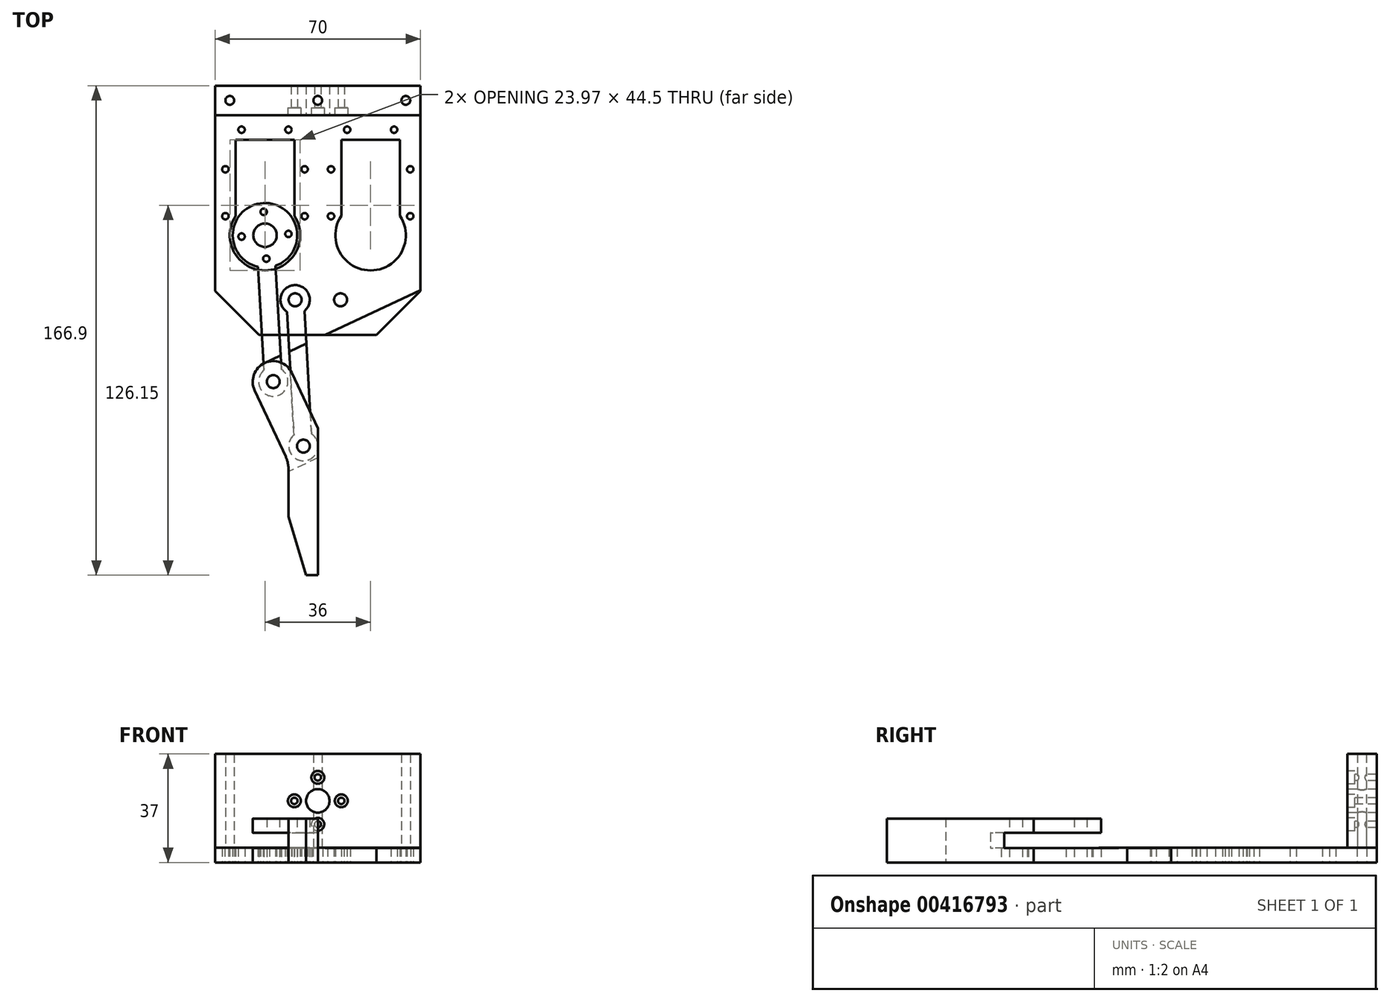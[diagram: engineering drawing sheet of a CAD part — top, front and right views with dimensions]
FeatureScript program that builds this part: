
annotation { "Feature Type Name" : "Feature", "Feature Type Description" : "" }
export const myFeature = defineFeature(function(context is Context, id is Id, definition is map)
    precondition{}
    {
        {
            var Q0;
            Q0=qCreatedBy(makeId("Top.planeOp"),FACE);
            var sketch = newSketch(context, id + "F0", { "sketchPlane" : qUnion([Q0])});
            skLineSegment(sketch, "E0.bottom", {"start": v(15, -15) * mm, "end": v(55, -15) * mm});
            skLineSegment(sketch, "E0.top", {"start": v(0, 70) * mm, "end": v(70, 70) * mm});
            skLineSegment(sketch, "E0.left", {"start": v(0, 0) * mm, "end": v(0, 70) * mm});
            skLineSegment(sketch, "E0.right", {"start": v(70, 0) * mm, "end": v(70, 70) * mm});
            skLineSegment(sketch, "E1.bottom", {"start": v(27, 51.5) * mm, "end": v(7, 51.5) * mm});
            skLineSegment(sketch, "E1.top", {"start": v(27, 25.63) * mm, "end": v(7, 25.63) * mm});
            skLineSegment(sketch, "E1.left", {"start": v(27, 51.5) * mm, "end": v(27, 25.63) * mm});
            skLineSegment(sketch, "E1.right", {"start": v(7, 51.5) * mm, "end": v(7, 25.63) * mm});
            skLineSegment(sketch, "E2", {"start": v(17, 51.5) * mm, "end": v(17, 19) * mm, "construction": true});
            skCircle(sketch, "E3", {"center": v(17, 19) * mm, "radius": 12 * mm});
            skPoint(sketch, "E4", {"position": v(30.5, 25.5) * mm});
            skPoint(sketch, "E5", {"position": v(30.5, 41.5) * mm});
            skPoint(sketch, "E6.MirrorP", {"position": v(3.5, 41.5) * mm});
            skPoint(sketch, "E7.MirrorP", {"position": v(3.5, 25.5) * mm});
            skPoint(sketch, "E8", {"position": v(25, 55) * mm});
            skPoint(sketch, "E9.MirrorP", {"position": v(9, 55) * mm});
            skPoint(sketch, "E10", {"position": v(30.5, 33.5) * mm});
            skPoint(sketch, "E11", {"position": v(30.5, 49.5) * mm});
            skPoint(sketch, "E12", {"position": v(3.5, 49.5) * mm});
            skPoint(sketch, "E13", {"position": v(3.5, 33.5) * mm});
            skLineSegment(sketch, "E14", {"start": v(0, 0) * mm, "end": v(15, -15) * mm});
            skLineSegment(sketch, "E15", {"start": v(55, -15) * mm, "end": v(70, 0) * mm});
            skPoint(sketch, "E16", {"position": v(27.26, -3) * mm});
            skLineSegment(sketch, "E17", {"start": v(35, 70) * mm, "end": v(35, 57.71) * mm, "construction": true});
            skPoint(sketch, "E18.MirrorP", {"position": v(53, 19) * mm});
            skPoint(sketch, "E19.MirrorP", {"position": v(42.74, -3) * mm});
            skPoint(sketch, "E20.MirrorP", {"position": v(66.5, 49.5) * mm});
            skPoint(sketch, "E21.MirrorP", {"position": v(66.5, 41.5) * mm});
            skPoint(sketch, "E22.MirrorP", {"position": v(66.5, 33.5) * mm});
            skPoint(sketch, "E23.MirrorP", {"position": v(66.5, 25.5) * mm});
            skPoint(sketch, "E24.MirrorP", {"position": v(39.5, 25.5) * mm});
            skPoint(sketch, "E25.MirrorP", {"position": v(39.5, 33.5) * mm});
            skPoint(sketch, "E26.MirrorP", {"position": v(39.5, 41.5) * mm});
            skPoint(sketch, "E27.MirrorP", {"position": v(39.5, 49.5) * mm});
            skPoint(sketch, "E28.MirrorP", {"position": v(45, 55) * mm});
            skPoint(sketch, "E29.MirrorP", {"position": v(61, 55) * mm});
            skLineSegment(sketch, "E30.MirrorCS", {"start": v(43, 51.5) * mm, "end": v(63, 51.5) * mm});
            skLineSegment(sketch, "E31.MirrorCS", {"start": v(43, 51.5) * mm, "end": v(43, 25.63) * mm});
            skLineSegment(sketch, "E32.MirrorCS", {"start": v(63, 51.5) * mm, "end": v(63, 25.63) * mm});
            skCircle(sketch, "E33.MirrorC", {"center": v(53, 19) * mm, "radius": 12 * mm});
            skLineSegment(sketch, "E34", {"start": v(27.26, -3) * mm, "end": v(17, 19) * mm, "construction": true});
            skPoint(sketch, "E35", {"position": v(5, 65) * mm});
            skPoint(sketch, "E36", {"position": v(65, 65) * mm});
            skPoint(sketch, "E37", {"position": v(35, 65) * mm});
            skSolve(sketch);
        }
        {
            var Q0;
            Q0 = qSketchRegion(id + "F0", true);
            extrude(context, id + "F1", {"entities" : qUnion([Q0]), "depth" : 5 * mm});
        }
        {
            var Q0;
            Q0=sQuery(id+"F0.wireOp",VERTEX,"E9.MirrorP");
            var Q1;
            Q1=sQuery(id+"F0.wireOp",VERTEX,"E6.MirrorP");
            var Q2;
            Q2=sQuery(id+"F0.wireOp",VERTEX,"E7.MirrorP");
            var Q3;
            Q3=sQuery(id+"F0.wireOp",VERTEX,"E4");
            var Q4;
            Q4=sQuery(id+"F0.wireOp",VERTEX,"E5");
            var Q5;
            Q5=sQuery(id+"F0.wireOp",VERTEX,"E24.MirrorP");
            var Q6;
            Q6=sQuery(id+"F0.wireOp",VERTEX,"E26.MirrorP");
            var Q7;
            Q7=sQuery(id+"F0.wireOp",VERTEX,"E21.MirrorP");
            var Q8;
            Q8=sQuery(id+"F0.wireOp",VERTEX,"E23.MirrorP");
            var Q9;
            Q9=sQuery(id+"F0.wireOp",VERTEX,"E29.MirrorP");
            var Q10;
            Q10=sQuery(id+"F0.wireOp",VERTEX,"E28.MirrorP");
            var Q11;
            Q11=sQuery(id+"F0.wireOp",VERTEX,"E8");
            var Q12;
            Q12=makeQuery(id+"F1.opExtrude","SWEPT_BODY",BODY,{"disambiguationData":[OSD([sQuery(id+"F0.wireOp",EDGE,"E0.bottom"),sQuery(id+"F0.wireOp",EDGE,"E0.top"),sQuery(id+"F0.wireOp",EDGE,"E0.left"),sQuery(id+"F0.wireOp",EDGE,"E0.right"),sQuery(id+"F0.wireOp",EDGE,"E1.bottom"),sQuery(id+"F0.wireOp",EDGE,"E1.left"),sQuery(id+"F0.wireOp",EDGE,"E1.right"),sQuery(id+"F0.wireOp",EDGE,"E14"),sQuery(id+"F0.wireOp",EDGE,"E15"),sQuery(id+"F0.wireOp",EDGE,"E30.MirrorCS"),sQuery(id+"F0.wireOp",EDGE,"E31.MirrorCS"),sQuery(id+"F0.wireOp",EDGE,"E32.MirrorCS"),sQuery(id+"F0.wireOp",EDGE,"E33.MirrorC"),sQuery(id+"F0.wireOp",EDGE,"E3")])]});
            hole(context, id + "F2", {"style" : HoleStyle.SIMPLE, "endStyle" : HoleEndStyle.THROUGH, "oppositeDirection" : true, "holeDiameter" : 2.2 * mm, "isTappedThrough" : true, "tappedDepth" : 6.2 * mm, "tapClearance" : 3, "locations" : qUnion([Q0, Q1, Q2, Q3, Q4, Q5, Q6, Q7, Q8, Q9, Q10, Q11]), "scope" : qUnion([Q12])});
        }
        {
            var Q0;
            Q0=sQuery(id+"F0.wireOp",VERTEX,"E16");
            var Q1;
            Q1=sQuery(id+"F0.wireOp",VERTEX,"E19.MirrorP");
            var Q2;
            Q2=makeQuery(id+"F1.opExtrude","SWEPT_BODY",BODY,{"disambiguationData":[OSD([sQuery(id+"F0.wireOp",EDGE,"E0.bottom"),sQuery(id+"F0.wireOp",EDGE,"E0.top"),sQuery(id+"F0.wireOp",EDGE,"E0.left"),sQuery(id+"F0.wireOp",EDGE,"E0.right"),sQuery(id+"F0.wireOp",EDGE,"E1.bottom"),sQuery(id+"F0.wireOp",EDGE,"E1.left"),sQuery(id+"F0.wireOp",EDGE,"E1.right"),sQuery(id+"F0.wireOp",EDGE,"E14"),sQuery(id+"F0.wireOp",EDGE,"E15"),sQuery(id+"F0.wireOp",EDGE,"E30.MirrorCS"),sQuery(id+"F0.wireOp",EDGE,"E31.MirrorCS"),sQuery(id+"F0.wireOp",EDGE,"E32.MirrorCS"),sQuery(id+"F0.wireOp",EDGE,"E33.MirrorC"),sQuery(id+"F0.wireOp",EDGE,"E3")])]});
            hole(context, id + "F3", {"style" : HoleStyle.SIMPLE, "endStyle" : HoleEndStyle.THROUGH, "oppositeDirection" : true, "standardTappedOrClearance" : lookupTablePath({ "standard" : "ISO", "fit" : "Normal", "size" : "M4", "type" : "Clearance" }), "standardBlindInLast" : lookupTablePath({ "fit" : "Standard", "standard" : "ISO", "size" : "M4", "type" : "Clearance" }), "holeDiameter" : 4.4 * mm, "isTappedThrough" : true, "tappedDepth" : 6.2 * mm, "tapClearance" : 3, "locations" : qUnion([Q0, Q1]), "scope" : qUnion([Q2])});
        }
        {
            var Q0;
            Q0=sQuery(id+"F0.wireOp",VERTEX,"E35");
            var Q1;
            Q1=sQuery(id+"F0.wireOp",VERTEX,"E37");
            var Q2;
            Q2=sQuery(id+"F0.wireOp",VERTEX,"E36");
            var Q3;
            Q3=makeQuery(id+"F1.opExtrude","SWEPT_BODY",BODY,{"disambiguationData":[OSD([sQuery(id+"F0.wireOp",EDGE,"E0.bottom"),sQuery(id+"F0.wireOp",EDGE,"E0.top"),sQuery(id+"F0.wireOp",EDGE,"E0.left"),sQuery(id+"F0.wireOp",EDGE,"E0.right"),sQuery(id+"F0.wireOp",EDGE,"E1.bottom"),sQuery(id+"F0.wireOp",EDGE,"E1.left"),sQuery(id+"F0.wireOp",EDGE,"E1.right"),sQuery(id+"F0.wireOp",EDGE,"E14"),sQuery(id+"F0.wireOp",EDGE,"E15"),sQuery(id+"F0.wireOp",EDGE,"E30.MirrorCS"),sQuery(id+"F0.wireOp",EDGE,"E31.MirrorCS"),sQuery(id+"F0.wireOp",EDGE,"E32.MirrorCS"),sQuery(id+"F0.wireOp",EDGE,"E33.MirrorC"),sQuery(id+"F0.wireOp",EDGE,"E3")])]});
            hole(context, id + "F4", {"style" : HoleStyle.SIMPLE, "endStyle" : HoleEndStyle.THROUGH, "oppositeDirection" : true, "standardTappedOrClearance" : lookupTablePath({ "standard" : "ISO", "fit" : "Normal", "size" : "M3", "type" : "Clearance" }), "standardBlindInLast" : lookupTablePath({ "fit" : "Standard", "standard" : "ISO", "size" : "M3", "type" : "Clearance" }), "holeDiameter" : 3.3 * mm, "isTappedThrough" : true, "tappedDepth" : 6.2 * mm, "tapClearance" : 3, "locations" : qUnion([Q0, Q1, Q2]), "scope" : qUnion([Q3])});
        }
        {
            var Q0;
            Q0=makeQuery(id+"F1.opExtrude","CAP_FACE",FACE,{"disambiguationData":[OSD([sQuery(id+"F0.wireOp",EDGE,"E0.bottom"),sQuery(id+"F0.wireOp",EDGE,"E0.top"),sQuery(id+"F0.wireOp",EDGE,"E0.left"),sQuery(id+"F0.wireOp",EDGE,"E0.right"),sQuery(id+"F0.wireOp",EDGE,"E1.bottom"),sQuery(id+"F0.wireOp",EDGE,"E1.left"),sQuery(id+"F0.wireOp",EDGE,"E1.right"),sQuery(id+"F0.wireOp",EDGE,"E14"),sQuery(id+"F0.wireOp",EDGE,"E15"),sQuery(id+"F0.wireOp",EDGE,"E30.MirrorCS"),sQuery(id+"F0.wireOp",EDGE,"E31.MirrorCS"),sQuery(id+"F0.wireOp",EDGE,"E32.MirrorCS"),sQuery(id+"F0.wireOp",EDGE,"E33.MirrorC"),sQuery(id+"F0.wireOp",EDGE,"E3")])],"isStart":false});
            var sketch = newSketch(context, id + "F5", { "sketchPlane" : qUnion([Q0])});
            skLineSegment(sketch, "E38.bottom", {"start": v(0, 70) * mm, "end": v(70, 70) * mm});
            skLineSegment(sketch, "E38.top", {"start": v(0, 60) * mm, "end": v(70, 60) * mm});
            skLineSegment(sketch, "E38.left", {"start": v(0, 70) * mm, "end": v(0, 60) * mm});
            skLineSegment(sketch, "E38.right", {"start": v(70, 70) * mm, "end": v(70, 60) * mm});
            skCircle(sketch, "E39", {"center": v(5, 65) * mm, "radius": 1.5 * mm});
            skCircle(sketch, "E40", {"center": v(35, 65) * mm, "radius": 1.5 * mm});
            skCircle(sketch, "E41", {"center": v(65, 65) * mm, "radius": 1.5 * mm});
            skSolve(sketch);
        }
        {
            var Q0;
            Q0=makeQuery(id+"F5.imprint","IMPRINT",FACE,{"disambiguationData":[TD([[makeQuery(id+"F5.imprint","IMPRINT",EDGE,{"derivedFrom":sQuery(id+"F5.wireOp",EDGE,"E39")}),-1.0]])]});
            var Q1;
            Q1=makeQuery(id+"F5.imprint","IMPRINT",FACE,{"disambiguationData":[TD([[makeQuery(id+"F5.imprint","IMPRINT",EDGE,{"derivedFrom":sQuery(id+"F5.wireOp",EDGE,"E40")}),-1.0]])]});
            var Q2;
            Q2=makeQuery(id+"F5.imprint","IMPRINT",FACE,{"disambiguationData":[TD([[makeQuery(id+"F5.imprint","IMPRINT",EDGE,{"derivedFrom":sQuery(id+"F5.wireOp",EDGE,"E38.bottom")}),-1.0]])]});
            var Q3;
            Q3=makeQuery(id+"F5.imprint","IMPRINT",FACE,{"disambiguationData":[TD([[makeQuery(id+"F5.imprint","IMPRINT",EDGE,{"derivedFrom":sQuery(id+"F5.wireOp",EDGE,"E41")}),-1.0]])]});
            extrude(context, id + "F6", {"entities" : qUnion([Q0, Q1, Q2, Q3]), "depth" : 32 * mm});
        }
        {
            var Q0;
            Q0=makeQuery(id+"F6.opExtrude","SWEPT_FACE",FACE,{"disambiguationData":[OSD([sQuery(id+"F5.wireOp",EDGE,"E38.top")])]});
            var sketch = newSketch(context, id + "F7", { "sketchPlane" : qUnion([Q0])});
            skCircle(sketch, "E42", {"center": v(35, 21) * mm, "radius": 8 * mm, "construction": true});
            skCircle(sketch, "E43", {"center": v(35, 29) * mm, "radius": 1.1 * mm});
            skCircle(sketch, "E44.1.0", {"center": v(27, 21) * mm, "radius": 1.1 * mm});
            skCircle(sketch, "E44.2.0", {"center": v(35, 13) * mm, "radius": 1.1 * mm});
            skCircle(sketch, "E44.3.0", {"center": v(43, 21) * mm, "radius": 1.1 * mm});
            skCircle(sketch, "E45", {"center": v(35, 21) * mm, "radius": 4 * mm});
            skSolve(sketch);
        }
        {
            var Q0;
            Q0 = qSketchRegion(id + "F7", true);
            extrude(context, id + "F8", {"entities" : qUnion([Q0]), "operationType" : NewBodyOperationType.REMOVE, "endBound" : BoundingType.THROUGH_ALL, "oppositeDirection" : true, "depth" : 25 * mm});
        }
        {
            var Q0;
            Q0=qCreatedBy(makeId("Top.planeOp"),FACE);
            var sketch = newSketch(context, id + "F9", { "sketchPlane" : qUnion([Q0])});
            skLineSegment(sketch, "E46", {"start": v(14, 18.83) * mm, "end": v(16.83, -31.09) * mm});
            skLineSegment(sketch, "E47", {"start": v(16.83, -31.09) * mm, "end": v(22.82, -30.75) * mm});
            skLineSegment(sketch, "E48", {"start": v(22.82, -30.75) * mm, "end": v(20, 19.17) * mm});
            skLineSegment(sketch, "E49", {"start": v(20, 19.17) * mm, "end": v(14, 18.83) * mm});
            skCircle(sketch, "E50", {"center": v(27.26, -3) * mm, "radius": 5 * mm});
            skCircle(sketch, "E51", {"center": v(19.82, -30.92) * mm, "radius": 5 * mm});
            skCircle(sketch, "E52", {"center": v(17, 19) * mm, "radius": 8 * mm, "construction": true});
            skLineSegment(sketch, "E53", {"start": v(24.26, -3.17) * mm, "end": v(30.25, -2.83) * mm});
            skLineSegment(sketch, "E54", {"start": v(24.26, -3.17) * mm, "end": v(27.09, -53.09) * mm});
            skLineSegment(sketch, "E55", {"start": v(27.09, -53.09) * mm, "end": v(33.08, -52.75) * mm});
            skLineSegment(sketch, "E56", {"start": v(33.08, -52.75) * mm, "end": v(30.25, -2.83) * mm});
            skCircle(sketch, "E57", {"center": v(30.08, -52.92) * mm, "radius": 5 * mm});
            skCircle(sketch, "E58.0", {"center": v(27.26, -3) * mm, "radius": 2.2 * mm});
            skCircle(sketch, "E59", {"center": v(30.08, -52.92) * mm, "radius": 2.2 * mm});
            skCircle(sketch, "E60", {"center": v(19.82, -30.92) * mm, "radius": 2.2 * mm});
            skLineSegment(sketch, "E61", {"start": v(30.08, -52.92) * mm, "end": v(19.82, -30.92) * mm, "construction": true});
            skCircle(sketch, "E62", {"center": v(17, 19) * mm, "radius": 11 * mm});
            skLineSegment(sketch, "E63", {"start": v(16.55, 26.99) * mm, "end": v(17.8, 4.71) * mm, "construction": true});
            skCircle(sketch, "E64", {"center": v(17, 19) * mm, "radius": 4 * mm});
            skCircle(sketch, "E65", {"center": v(16.55, 26.99) * mm, "radius": 1.1 * mm});
            skCircle(sketch, "E66.1.0", {"center": v(9.01, 18.55) * mm, "radius": 1.1 * mm});
            skCircle(sketch, "E66.2.0", {"center": v(17.45, 11.01) * mm, "radius": 1.1 * mm});
            skCircle(sketch, "E66.3.0", {"center": v(24.99, 19.45) * mm, "radius": 1.1 * mm});
            skSolve(sketch);
        }
        {
            var Q0;
            Q0=makeQuery(id+"F9.imprint","IMPRINT",FACE,{"disambiguationData":[TD([[makeQuery(id+"F9.imprint","IMPRINT",EDGE,{"derivedFrom":sQuery(id+"F9.wireOp",EDGE,"648b47fd-c98e-4e7c-a0a6-51eef2966ebb.1.0")}),-1.0]])]});
            var Q1;
            {var subQ1=sQuery(id+"F9.wireOp",EDGE,"E47");var subQ7=sQuery(id+"F9.wireOp",EDGE,"E46");var subQ8=makeQuery(id+"F9.imprint","INTERSECT",VERTEX,{"derivedFrom":[subQ7,subQ1]});Q1=makeQuery(id+"F9.imprint","IMPRINT",FACE,{"disambiguationData":[TD([[makeQuery(id+"F9.imprint","IMPRINT",EDGE,{"disambiguationData":[TD([[subQ8,1.0]])],"derivedFrom":subQ7}),-1.0]])]});}
            var Q2;
            {var subQ1=sQuery(id+"F9.wireOp",EDGE,"E47");var subQ7=sQuery(id+"F9.wireOp",EDGE,"E46");var subQ8=makeQuery(id+"F9.imprint","INTERSECT",VERTEX,{"derivedFrom":[subQ7,subQ1]});Q2=makeQuery(id+"F9.imprint","IMPRINT",FACE,{"disambiguationData":[TD([[makeQuery(id+"F9.imprint","IMPRINT",EDGE,{"disambiguationData":[TD([[subQ8,1.0]])],"derivedFrom":subQ7}),1.0]])]});}
            var Q3;
            {var subQ0=sQuery(id+"F9.wireOp",EDGE,"E54");var subQ1=sQuery(id+"F9.wireOp",EDGE,"E50");var subQ2=makeQuery(id+"F9.imprint","INTERSECT",VERTEX,{"derivedFrom":[subQ1,subQ0]});Q3=makeQuery(id+"F9.imprint","IMPRINT",FACE,{"disambiguationData":[TD([[makeQuery(id+"F9.imprint","IMPRINT",EDGE,{"disambiguationData":[TD([[subQ2,-1.0]])],"derivedFrom":subQ1}),-1.0]])]});}
            var Q4;
            {var subQ0=sQuery(id+"F9.wireOp",EDGE,"E54");var subQ3=sQuery(id+"F9.wireOp",EDGE,"E50");var subQ4=makeQuery(id+"F9.imprint","INTERSECT",VERTEX,{"derivedFrom":[subQ3,subQ0]});Q4=makeQuery(id+"F9.imprint","IMPRINT",FACE,{"disambiguationData":[TD([[makeQuery(id+"F9.imprint","IMPRINT",EDGE,{"disambiguationData":[TD([[subQ4,1.0]])],"derivedFrom":subQ3}),1.0]])]});}
            var Q5;
            {var subQ0=sQuery(id+"F9.wireOp",EDGE,"E54");var subQ3=sQuery(id+"F9.wireOp",EDGE,"E50");var subQ4=makeQuery(id+"F9.imprint","INTERSECT",VERTEX,{"derivedFrom":[subQ3,subQ0]});Q5=makeQuery(id+"F9.imprint","IMPRINT",FACE,{"disambiguationData":[TD([[makeQuery(id+"F9.imprint","IMPRINT",EDGE,{"disambiguationData":[TD([[subQ4,-1.0]])],"derivedFrom":subQ3}),1.0]])]});}
            var Q6;
            {var subQ1=sQuery(id+"F9.wireOp",EDGE,"E55");var subQ7=sQuery(id+"F9.wireOp",EDGE,"E54");var subQ8=makeQuery(id+"F9.imprint","INTERSECT",VERTEX,{"derivedFrom":[subQ7,subQ1]});Q6=makeQuery(id+"F9.imprint","IMPRINT",FACE,{"disambiguationData":[TD([[makeQuery(id+"F9.imprint","IMPRINT",EDGE,{"disambiguationData":[TD([[subQ8,1.0]])],"derivedFrom":subQ7}),1.0]])]});}
            var Q7;
            {var subQ1=sQuery(id+"F9.wireOp",EDGE,"E55");var subQ7=sQuery(id+"F9.wireOp",EDGE,"E54");var subQ8=makeQuery(id+"F9.imprint","INTERSECT",VERTEX,{"derivedFrom":[subQ7,subQ1]});Q7=makeQuery(id+"F9.imprint","IMPRINT",FACE,{"disambiguationData":[TD([[makeQuery(id+"F9.imprint","IMPRINT",EDGE,{"disambiguationData":[TD([[subQ8,1.0]])],"derivedFrom":subQ7}),-1.0]])]});}
            var Q8;
            {var subQ0=sQuery(id+"F9.wireOp",EDGE,"E62");var subQ1=sQuery(id+"F9.wireOp",EDGE,"E46");var subQ2=makeQuery(id+"F9.imprint","INTERSECT",VERTEX,{"derivedFrom":[subQ1,subQ0]});Q8=makeQuery(id+"F9.imprint","IMPRINT",FACE,{"disambiguationData":[TD([[makeQuery(id+"F9.imprint","IMPRINT",EDGE,{"disambiguationData":[TD([[subQ2,-1.0]])],"derivedFrom":subQ1}),1.0]])]});}
            var Q9;
            Q9=makeQuery(id+"F9.imprint","IMPRINT",FACE,{"disambiguationData":[TD([[makeQuery(id+"F9.imprint","IMPRINT",EDGE,{"derivedFrom":sQuery(id+"F9.wireOp",EDGE,"E65")}),-1.0]])]});
            var Q10;
            Q10=makeQuery(id+"F9.imprint","IMPRINT",FACE,{"disambiguationData":[TD([[makeQuery(id+"F9.imprint","IMPRINT",EDGE,{"derivedFrom":sQuery(id+"F9.wireOp",EDGE,"E66.2.0")}),-1.0]])]});
            extrude(context, id + "F10", {"entities" : qUnion([Q0, Q1, Q2, Q3, Q4, Q5, Q6, Q7, Q8, Q9, Q10]), "depth" : 5 * mm});
        }
        {
            var Q0;
            Q0=qCreatedBy(makeId("Top.planeOp"),FACE);
            var sketch = newSketch(context, id + "F11", { "sketchPlane" : qUnion([Q0])});
            skLineSegment(sketch, "E67", {"start": v(35, -46.9) * mm, "end": v(23.2, -21.62) * mm});
            skLineSegment(sketch, "E68", {"start": v(10.52, -27.53) * mm, "end": v(25, -58.58) * mm});
            skLineSegment(sketch, "E69", {"start": v(23.2, -21.62) * mm, "end": v(10.52, -27.53) * mm});
            skLineSegment(sketch, "E70", {"start": v(35, -46.9) * mm, "end": v(35, -96.9) * mm});
            skLineSegment(sketch, "E71", {"start": v(35, -96.9) * mm, "end": v(31, -96.9) * mm});
            skLineSegment(sketch, "E72", {"start": v(25, -58.58) * mm, "end": v(25, -76.9) * mm});
            skLineSegment(sketch, "E73", {"start": v(25, -76.9) * mm, "end": v(31, -96.9) * mm});
            skCircle(sketch, "E74.0", {"center": v(30.08, -52.92) * mm, "radius": 2.2 * mm});
            skCircle(sketch, "E74.1", {"center": v(19.82, -30.92) * mm, "radius": 2.2 * mm});
            skSolve(sketch);
        }
        {
            var Q0;
            Q0 = qSketchRegion(id + "F11", true);
            extrude(context, id + "F12", {"entities" : qUnion([Q0]), "depth" : 15 * mm});
        }
        {
            var Q0;
            Q0=makeQuery(id+"F12.opExtrude","SWEPT_FACE",FACE,{"disambiguationData":[OSD([sQuery(id+"F11.wireOp",EDGE,"E68")])]});
            var sketch = newSketch(context, id + "F13", { "sketchPlane" : qUnion([Q0])});
            skLineSegment(sketch, "E75.bottom", {"start": v(29.4, 4.9) * mm, "end": v(66.4, 4.9) * mm});
            skLineSegment(sketch, "E75.top", {"start": v(29.4, 10.1) * mm, "end": v(66.4, 10.1) * mm});
            skLineSegment(sketch, "E75.left", {"start": v(29.4, 4.9) * mm, "end": v(29.4, 10.1) * mm});
            skLineSegment(sketch, "E75.right", {"start": v(66.4, 4.9) * mm, "end": v(66.4, 10.1) * mm});
            skSolve(sketch);
        }
        {
            var Q0;
            Q0 = qSketchRegion(id + "F13", true);
            extrude(context, id + "F14", {"entities" : qUnion([Q0]), "operationType" : NewBodyOperationType.REMOVE, "endBound" : BoundingType.THROUGH_ALL, "oppositeDirection" : true, "depth" : 25 * mm, "hasSecondDirection" : true, "secondDirectionBound" : SecondDirectionBoundingType.THROUGH_ALL, "secondDirectionOppositeDirection" : false, "secondDirectionDepth" : 25 * mm});
        }
        {
            var Q0;
            {var subQ0=sQuery(id+"F11.wireOp",EDGE,"E69");var subQ1=sQuery(id+"F11.wireOp",EDGE,"E68");Q0=makeQuery(id+"F14.boolean.opBoolean","SPLIT",EDGE,{"disambiguationData":[TD([makeQuery(id+"F14.opExtrude","SWEPT_FACE",FACE,{"disambiguationData":[OSD([sQuery(id+"F13.wireOp",EDGE,"E75.top")])]})])],"derivedFrom":makeQuery(id+"F12.opExtrude","SWEPT_EDGE",EDGE,{"disambiguationData":[OSD([subQ1,subQ0])]})});}
            var Q1;
            {var subQ0=sQuery(id+"F11.wireOp",EDGE,"E69");var subQ1=sQuery(id+"F11.wireOp",EDGE,"E68");Q1=makeQuery(id+"F14.boolean.opBoolean","SPLIT",EDGE,{"disambiguationData":[TD([makeQuery(id+"F14.opExtrude","SWEPT_FACE",FACE,{"disambiguationData":[OSD([sQuery(id+"F13.wireOp",EDGE,"E75.bottom")])]})])],"derivedFrom":makeQuery(id+"F12.opExtrude","SWEPT_EDGE",EDGE,{"disambiguationData":[OSD([subQ1,subQ0])]})});}
            var Q2;
            {var subQ0=sQuery(id+"F11.wireOp",EDGE,"E67");var subQ1=sQuery(id+"F11.wireOp",EDGE,"E69");Q2=makeQuery(id+"F14.boolean.opBoolean","SPLIT",EDGE,{"disambiguationData":[TD([makeQuery(id+"F14.opExtrude","SWEPT_FACE",FACE,{"disambiguationData":[OSD([sQuery(id+"F13.wireOp",EDGE,"E75.top")])]})])],"derivedFrom":makeQuery(id+"F12.opExtrude","SWEPT_EDGE",EDGE,{"disambiguationData":[OSD([subQ0,subQ1])]})});}
            var Q3;
            {var subQ0=sQuery(id+"F11.wireOp",EDGE,"E67");var subQ1=sQuery(id+"F11.wireOp",EDGE,"E69");Q3=makeQuery(id+"F14.boolean.opBoolean","SPLIT",EDGE,{"disambiguationData":[TD([makeQuery(id+"F14.opExtrude","SWEPT_FACE",FACE,{"disambiguationData":[OSD([sQuery(id+"F13.wireOp",EDGE,"E75.bottom")])]})])],"derivedFrom":makeQuery(id+"F12.opExtrude","SWEPT_EDGE",EDGE,{"disambiguationData":[OSD([subQ0,subQ1])]})});}
            fillet(context, id + "F15", {"entities" : qUnion([Q0, Q1, Q2, Q3]), "radius" : 7 * mm, "tangentPropagation" : true, "allowEdgeOverflow" : false});
        }
        {
            var Q0;
            {var subQ0=sQuery(id+"F11.wireOp",EDGE,"E72");var subQ1=sQuery(id+"F11.wireOp",EDGE,"E68");Q0=makeQuery(id+"F14.boolean.opBoolean","SPLIT",EDGE,{"disambiguationData":[TD([makeQuery(id+"F14.opExtrude","SWEPT_FACE",FACE,{"disambiguationData":[OSD([sQuery(id+"F13.wireOp",EDGE,"E75.top")])]})])],"derivedFrom":makeQuery(id+"F12.opExtrude","SWEPT_EDGE",EDGE,{"disambiguationData":[OSD([subQ1,subQ0])]})});}
            var Q1;
            {var subQ0=sQuery(id+"F11.wireOp",EDGE,"E72");var subQ1=sQuery(id+"F11.wireOp",EDGE,"E68");Q1=makeQuery(id+"F14.boolean.opBoolean","SPLIT",EDGE,{"disambiguationData":[TD([makeQuery(id+"F14.opExtrude","SWEPT_FACE",FACE,{"disambiguationData":[OSD([sQuery(id+"F13.wireOp",EDGE,"E75.bottom")])]})])],"derivedFrom":makeQuery(id+"F12.opExtrude","SWEPT_EDGE",EDGE,{"disambiguationData":[OSD([subQ1,subQ0])]})});}
            fillet(context, id + "F16", {"entities" : qUnion([Q0, Q1]), "radius" : 10 * mm, "tangentPropagation" : true, "allowEdgeOverflow" : false});
        }
        {
            var Q0;
            Q0=sQuery(id+"F7.wireOp",VERTEX,"E43.center");
            var Q1;
            Q1=sQuery(id+"F7.wireOp",VERTEX,"E44.3.0.center");
            var Q2;
            Q2=sQuery(id+"F7.wireOp",VERTEX,"E44.2.0.center");
            var Q3;
            Q3=sQuery(id+"F7.wireOp",VERTEX,"E44.1.0.center");
            var Q4;
            Q4=makeQuery(id+"F6.opExtrude","SWEPT_BODY",BODY,{"disambiguationData":[OSD([sQuery(id+"F5.wireOp",EDGE,"E38.bottom"),sQuery(id+"F5.wireOp",EDGE,"E38.top"),sQuery(id+"F5.wireOp",EDGE,"E38.left"),sQuery(id+"F5.wireOp",EDGE,"E38.right"),sQuery(id+"F5.wireOp",EDGE,"E39"),sQuery(id+"F5.wireOp",EDGE,"E40"),sQuery(id+"F5.wireOp",EDGE,"E41")])]});
            hole(context, id + "F17", {"style" : HoleStyle.C_BORE, "endStyle" : HoleEndStyle.THROUGH, "holeDiameter" : 2.2 * mm, "cBoreDiameter" : 4.4 * mm, "cBoreDepth" : 2.5 * mm, "isTappedThrough" : true, "tappedDepth" : 6.2 * mm, "tapClearance" : 3, "locations" : qUnion([Q0, Q1, Q2, Q3]), "scope" : qUnion([Q4])});
        }
    });
